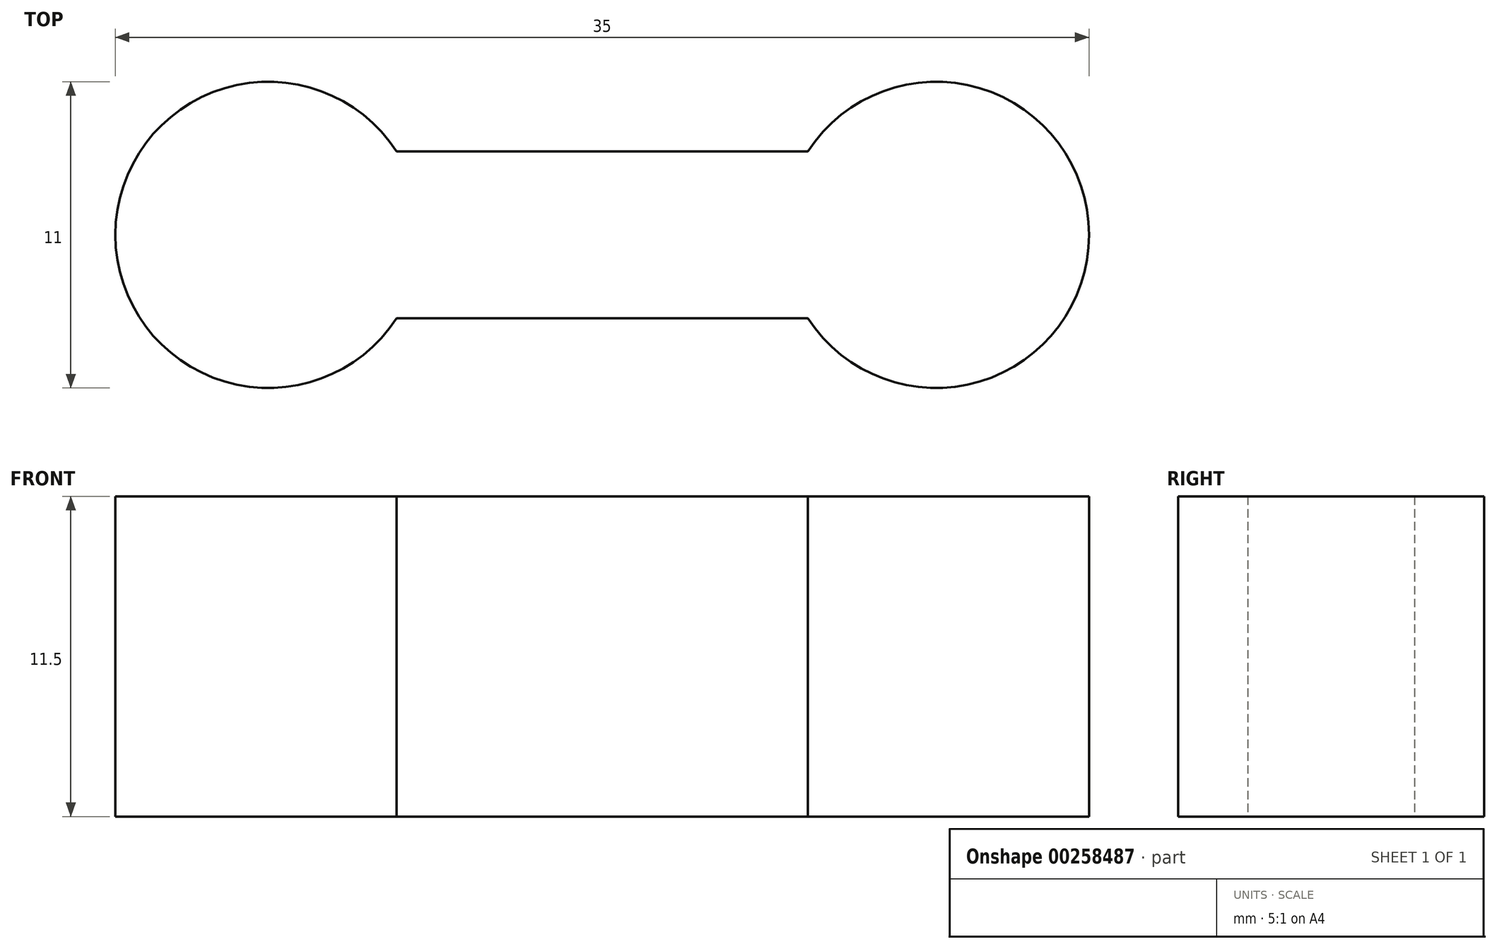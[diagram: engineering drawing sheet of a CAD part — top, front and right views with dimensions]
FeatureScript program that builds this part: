
annotation { "Feature Type Name" : "Feature", "Feature Type Description" : "" }
export const myFeature = defineFeature(function(context is Context, id is Id, definition is map)
    precondition{}
    {
        {
            var Q0;
            Q0=qCreatedBy(makeId("Top.planeOp"),FACE);
            var sketch = newSketch(context, id + "F0", { "sketchPlane" : qUnion([Q0])});
            skCircle(sketch, "E0", {"center": v(0, 0) * mm, "radius": 5.5 * mm});
            skCircle(sketch, "E1", {"center": v(24, 0) * mm, "radius": 5.5 * mm});
            skLineSegment(sketch, "E2", {"start": v(4.6, 3) * mm, "end": v(19.4, 3) * mm});
            skLineSegment(sketch, "E3", {"start": v(4.6, -3) * mm, "end": v(19.4, -3) * mm});
            skSolve(sketch);
        }
        {
            var Q0;
            {var subQ0=sQuery(id+"F0.wireOp",EDGE,"E0");var subQ1=makeQuery(id+"F0.imprint","INTERSECT",VERTEX,{"derivedFrom":[subQ0,sQuery(id+"F0.wireOp",EDGE,"E2")]});Q0=makeQuery(id+"F0.imprint","IMPRINT",FACE,{"disambiguationData":[TD([[makeQuery(id+"F0.imprint","IMPRINT",EDGE,{"disambiguationData":[TD([[subQ1,-1.0]])],"derivedFrom":subQ0}),1.0]])]});}
            var Q1;
            {var subQ0=sQuery(id+"F0.wireOp",EDGE,"E2");Q1=makeQuery(id+"F0.imprint","IMPRINT",FACE,{"disambiguationData":[TD([[makeQuery(id+"F0.imprint","IMPRINT",EDGE,{"derivedFrom":subQ0}),-1.0]])]});}
            var Q2;
            {var subQ0=sQuery(id+"F0.wireOp",EDGE,"E1");var subQ1=makeQuery(id+"F0.imprint","INTERSECT",VERTEX,{"derivedFrom":[subQ0,sQuery(id+"F0.wireOp",EDGE,"E2")]});Q2=makeQuery(id+"F0.imprint","IMPRINT",FACE,{"disambiguationData":[TD([[makeQuery(id+"F0.imprint","IMPRINT",EDGE,{"disambiguationData":[TD([[subQ1,-1.0]])],"derivedFrom":subQ0}),1.0]])]});}
            extrude(context, id + "F1", {"entities" : qUnion([Q0, Q1, Q2]), "depth" : 11.5 * mm});
        }
    });
